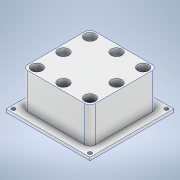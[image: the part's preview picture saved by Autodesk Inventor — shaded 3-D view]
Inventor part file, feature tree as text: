
AUTODESK INVENTOR PART (.ipt)
format: ipt  version: 2020 (Build 240168000, 168)  size: 218,624 bytes
history: native  units: mm
features: thread x4, extrude x3, sketch x3
ambient origin geometry x8: Origin, YZ Plane, XZ Plane, XY Plane, X Axis, Y Axis, Z Axis, Center Point
bodies: Solid1 (feature_tree)
feature tree (10):
  extrude  "Extrusion1"  Depth=66.0mm
  extrude  "Extrusion2"  Depth=5.0mm
  extrude  "Extrusion4"  Depth=10.0mm
  thread  "Thread5"  [1 undecoded]
  thread  "Thread6"  [1 undecoded]
  thread  "Thread7"  [1 undecoded]
  thread  "Thread8"  [1 undecoded]
  sketch  "Sketch1"  dims[d0=66.0mm d1=66.0mm]
  sketch  "Sketch2"  dims[d2=35.0mm d3=0.0mm d4=5.0mm]
  sketch  "Sketch4"  dims[d8=10.0mm d9=10.0mm d10=10.7mm d11=26.0mm d12=26.0mm d13=30.0mm d15=26.0mm d16=30.0mm d18=26.0mm d21=35.0mm d22=0.0mm d28=75.0mm d29=75.0mm d31=82.0mm d33=3.0mm d34=0.0mm d56=3.7mm d66=20.0mm d68=75.0mm d69=20.0mm d71=75.0mm d74=5.5mm d75=0.0mm d76=5.5mm d77=0.0mm d78=5.5mm d79=0.0mm d80=5.5mm d81=0.0mm]
note: 4 required parameter values undecoded (feature->parameter linkage not recoverable at this tier; creation-order binding heuristic only, values carry confidence <= 0.55)
